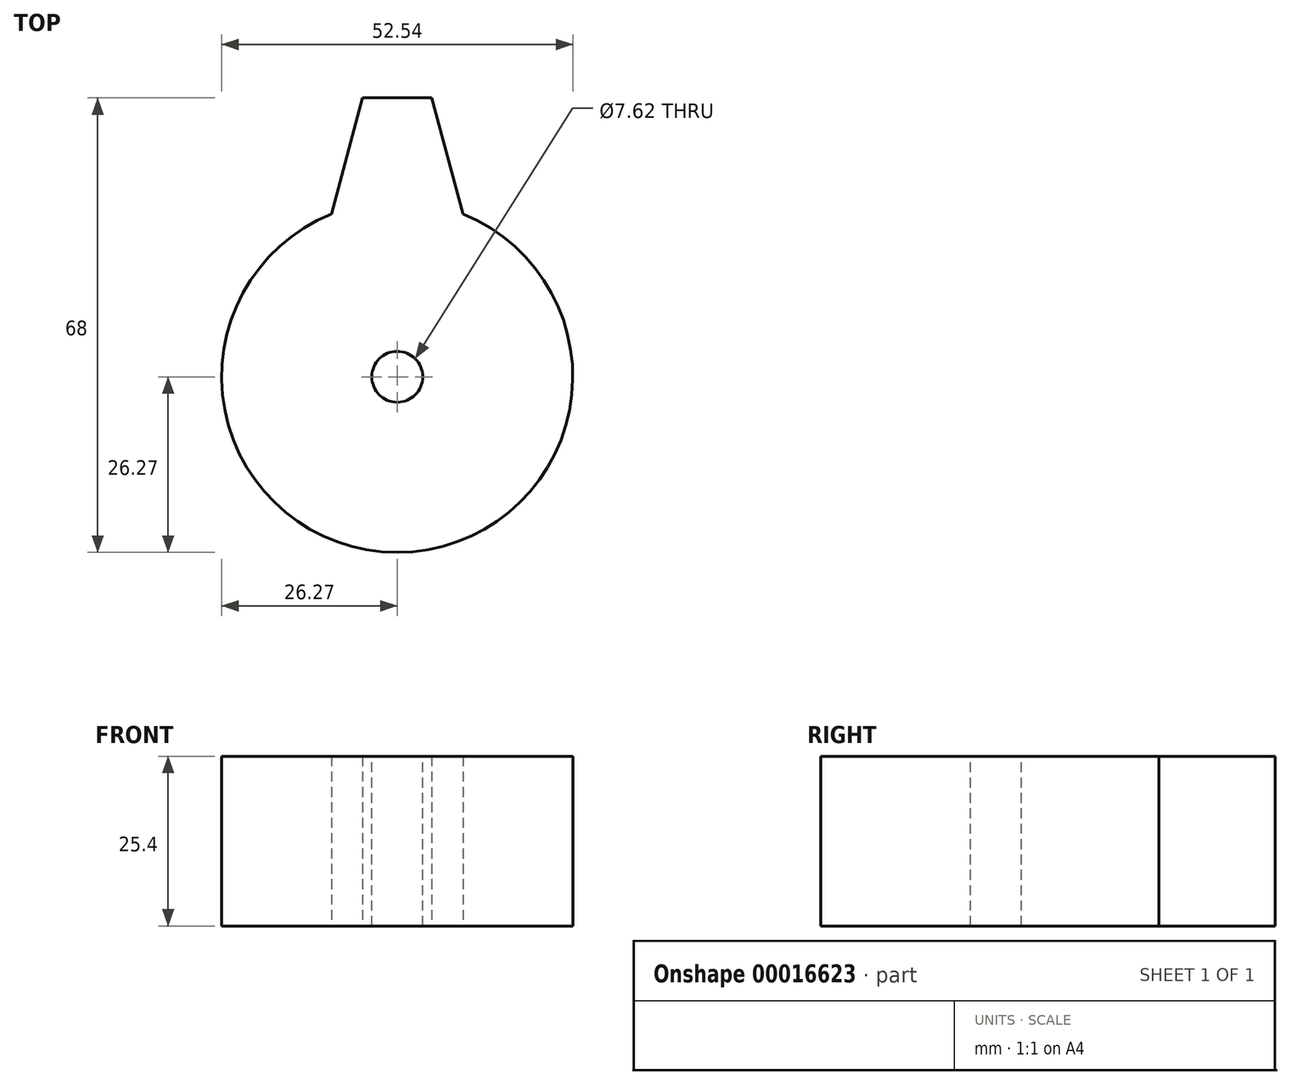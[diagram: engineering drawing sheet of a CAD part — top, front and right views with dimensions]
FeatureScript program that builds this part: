
annotation { "Feature Type Name" : "Feature", "Feature Type Description" : "" }
export const myFeature = defineFeature(function(context is Context, id is Id, definition is map)
    precondition{}
    {
        {
            var Q0;
            Q0=qCreatedBy(makeId("Top.planeOp"),FACE);
            var sketch = newSketch(context, id + "F0", { "sketchPlane" : qUnion([Q0])});
            skCircle(sketch, "E0", {"center": v(0, 0) * mm, "radius": 26.27 * mm});
            skLineSegment(sketch, "E1", {"start": v(0, 0) * mm, "end": v(0, 26.27) * mm, "construction": true});
            skLineSegment(sketch, "E2", {"start": v(-9.86, 24.35) * mm, "end": v(-5.19, 41.73) * mm});
            skLineSegment(sketch, "E3", {"start": v(-5.19, 41.73) * mm, "end": v(0, 41.73) * mm});
            skLineSegment(sketch, "E4.MirrorCS", {"start": v(9.86, 24.35) * mm, "end": v(5.19, 41.73) * mm});
            skLineSegment(sketch, "E5.MirrorCS", {"start": v(5.19, 41.73) * mm, "end": v(0, 41.73) * mm});
            skSolve(sketch);
        }
        {
            var Q0;
            Q0 = qSketchRegion(id + "F0", true);
            extrude(context, id + "F1", {"entities" : qUnion([Q0]), "depth" : 25.4 * mm});
        }
        {
            var Q0;
            Q0=makeQuery(id+"F1.opExtrude","CAP_FACE",FACE,{"disambiguationData":[OSD([sQuery(id+"F0.wireOp",EDGE,"E0"),sQuery(id+"F0.wireOp",EDGE,"E2"),sQuery(id+"F0.wireOp",EDGE,"E3"),sQuery(id+"F0.wireOp",EDGE,"E4.MirrorCS"),sQuery(id+"F0.wireOp",EDGE,"E5.MirrorCS")])],"isStart":false});
            var sketch = newSketch(context, id + "F2", { "sketchPlane" : qUnion([Q0])});
            skCircle(sketch, "E6", {"center": v(0, 0) * mm, "radius": 3.81 * mm});
            skSolve(sketch);
        }
        {
            var Q0;
            Q0 = qSketchRegion(id + "F2", true);
            extrude(context, id + "F3", {"entities" : qUnion([Q0]), "operationType" : NewBodyOperationType.REMOVE, "endBound" : BoundingType.THROUGH_ALL, "oppositeDirection" : true, "depth" : 25.4 * mm});
        }
    });
